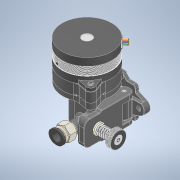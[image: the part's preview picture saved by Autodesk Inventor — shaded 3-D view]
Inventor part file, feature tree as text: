
AUTODESK INVENTOR PART (.ipt)
format: ipt  version: 2022 (Build 260153000, 153)  size: 24,311,296 bytes
history: native  units: in
note: dims shown in document units (in); Inventor stores cm internally (conversion verified against a paired STEP export)
features: other x74, sketch x4
ambient origin geometry x8: Origin, YZ Plane, XZ Plane, XY Plane, X Axis, Y Axis, Z Axis, Center Point
bodies: Solid1 (feature_tree), Solid2 (feature_tree), Solid3 (feature_tree), Solid4 (feature_tree), Solid5 (feature_tree), Solid6 (feature_tree), Solid7 (feature_tree), Solid8 (feature_tree), Solid9 (feature_tree), Solid10 (feature_tree), Solid11 (feature_tree), Solid12 (feature_tree), Solid13 (feature_tree), Solid14 (feature_tree), Solid15 (feature_tree), Solid16 (feature_tree), Solid17 (feature_tree), Solid18 (feature_tree), Solid19 (feature_tree), Solid20 (feature_tree), Solid21 (feature_tree), Solid22 (feature_tree), Solid23 (feature_tree), Solid24 (feature_tree), Solid25 (feature_tree), Solid26 (feature_tree), Solid27 (feature_tree), Solid28 (feature_tree), Solid29 (feature_tree), Solid30 (feature_tree), Solid31 (feature_tree), Solid32 (feature_tree), Solid33 (feature_tree), Solid34 (feature_tree), Solid35 (feature_tree), Solid36 (feature_tree), Solid37 (feature_tree), Solid38 (feature_tree), Solid39 (feature_tree), Solid40 (feature_tree), Solid41 (feature_tree), Solid42 (feature_tree), Solid43 (feature_tree), Solid44 (feature_tree), Solid45 (feature_tree), Solid46 (feature_tree), Solid47 (feature_tree), Solid48 (feature_tree), Solid49 (feature_tree), Solid50 (feature_tree), Solid51 (feature_tree), Solid52 (feature_tree), Solid53 (feature_tree), Solid54 (feature_tree), Solid55 (feature_tree), Solid56 (feature_tree), Solid57 (feature_tree), Solid58 (feature_tree), Solid59 (feature_tree), Solid60 (feature_tree), Solid61 (feature_tree), Solid62 (feature_tree), Solid63 (feature_tree), Solid64 (feature_tree), Solid65 (feature_tree), Solid66 (feature_tree), Solid67 (feature_tree), Solid68 (feature_tree), Solid69 (feature_tree), Solid70 (feature_tree), Solid71 (feature_tree), Solid73 (feature_tree), Solid74 (feature_tree), Solid76 (feature_tree)
feature tree (78):
  sketch  "Sketch1"
  sketch  "Sketch2"
  sketch  "Sketch3"
  sketch  "Sketch4"
  other  "LatchShaft_1:1"
  other  "SpiderShaft_1:1"
  other  "FlyGear_1:1"
  other  "MotorGear_1:1"
  other  "Housing 1.5_1:1"
  other  "6mm Press_Fitting_1:1"
  other  "T10 SpurGear_1:1"
  other  "Component14_1:1"
  other  "Component13_1:1"
  other  "Component7_1:1"
  other  "Component4_1:1"
  other  "Component3_1:1"
  other  "Component18_1:1"
  other  "Component6_1:1"
  other  "Component12_1:1"
  other  "Component15_1:1"
  other  "Component17_1:1"
  other  "Component5_1:1"
  other  "Component8_1:1"
  other  "Component11_1:1"
  other  "Component10_1:1"
  other  "Component16_1:1"
  other  "Component9_1:1"
  other  "92125A138_1:1"
  other  "90940A412_1:1"
  other  "Spring v1_1:1"
  other  "KnurledNut_1:1"
  other  "Latch_1:1"
  other  "F688ZZ_1:1"
  other  "F688ZZ (1)_1:1"
  other  "F688ZZ (2)_1:1"
  other  "F688ZZ (3)_1:1"
  other  "spur gear_gb_GB - Spur gear 0.5M 27T 20PA 4FW ---S27A75H50L5.0N_1:1"
  other  "MR85_1:1"
  other  "F688ZZ (4)_1:1"
  other  "F688ZZ (5)_1:1"
  other  "F688ZZ (6)_1:1"
  other  "Gear Housing (65 teeth)_1:1"
  other  "F688ZZ (7)_1:1"
  other  "F688ZZ (8)_1:1"
  other  "F688ZZ (9)_1:1"
  other  "F688ZZ (10)_1:1"
  other  "F688ZZ (11)_1:1"
  other  "F688ZZ (12)_1:1"
  other  "_MR148ZZ Ball_1:1"
  other  "_MR148ZZ Inner Ring_1:1"
  other  "_MR148ZZ Shield2_1:1"
  other  "_MR148ZZ Outer Ring_1:1"
  other  "_MR148ZZ Shield1_1:1"
  other  "_MR148ZZ Ball_2:1"
  other  "_MR148ZZ Ball_3:1"
  other  "_MR148ZZ Ball_4:1"
  other  "_MR148ZZ Ball_5:1"
  other  "_MR148ZZ Ball_6:1"
  other  "_MR148ZZ Ball_7:1"
  other  "_MR148ZZ Ball_8:1"
  other  "_MR148ZZ Ball_9:1"
  other  "_MR148ZZ Ball_10:1"
  other  "_MR148ZZ Ball_11:1"
  other  "_MR148ZZ Ball_12:1"
  other  "_MR148ZZ Ball_13:1"
  other  "_MR148ZZ Ball_14:1"
  other  "F688ZZ (13)_1:1"
  other  "F688ZZ (14)_1:1"
  other  "F688ZZ (15)_1:1"
  other  "spur gear_gb_GB - Spur gear 0.5M 27T 20PA 4FW ---S27A75H50L5.0N_2:1"
  other  "MR85_2:1"
  other  "spur gear_gb_GB - Spur gear 0.5M 27T 20PA 4FW ---S27A75H50L5.0N_3:1"
  other  "MR85_3:1"
  other  "insert M3 v1_1:1"
  other  "92095A119_1:1"
  other  "LatchSleve_1:1"
  other  "insert M3 v1 (1)_1:1"
  other  "92095A119_2:1"
